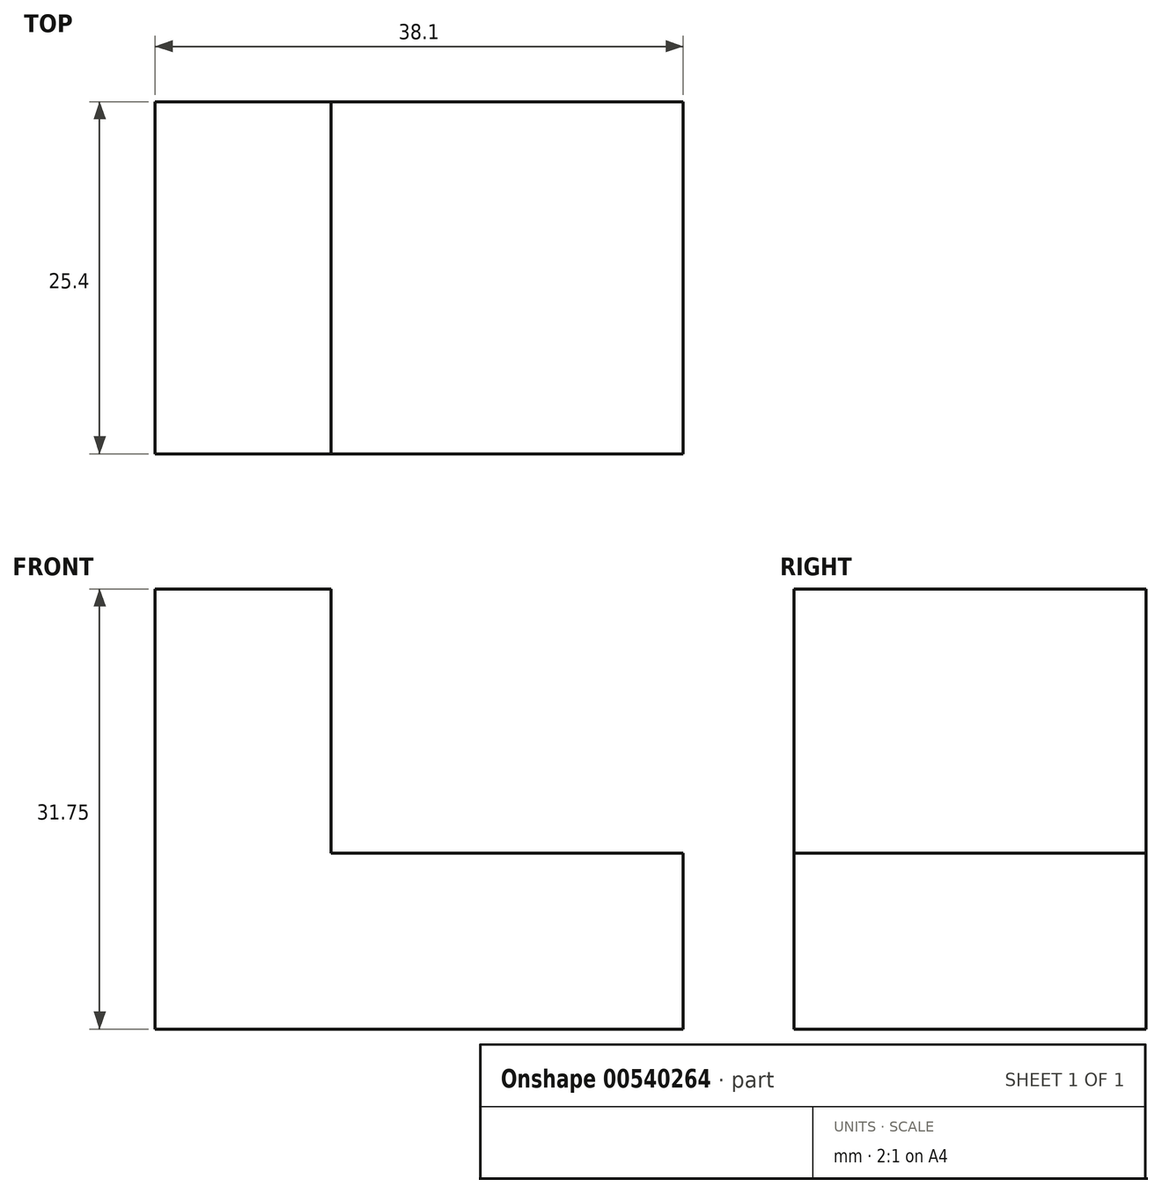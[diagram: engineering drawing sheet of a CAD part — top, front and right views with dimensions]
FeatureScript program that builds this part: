
annotation { "Feature Type Name" : "Feature", "Feature Type Description" : "" }
export const myFeature = defineFeature(function(context is Context, id is Id, definition is map)
    precondition{}
    {
        {
            var Q0;
            Q0=qCreatedBy(makeId("Front.planeOp"),FACE);
            var sketch = newSketch(context, id + "F0", { "sketchPlane" : qUnion([Q0])});
            skLineSegment(sketch, "E0", {"start": v(-68.75, 31.75) * mm, "end": v(-68.75, 0) * mm});
            skLineSegment(sketch, "E1", {"start": v(-68.75, 0) * mm, "end": v(-30.65, 0) * mm});
            skLineSegment(sketch, "E2", {"start": v(-30.65, 0) * mm, "end": v(-30.65, 12.7) * mm});
            skLineSegment(sketch, "E3", {"start": v(-30.65, 12.7) * mm, "end": v(-56.05, 12.7) * mm});
            skLineSegment(sketch, "E4", {"start": v(-56.05, 12.7) * mm, "end": v(-56.05, 31.75) * mm});
            skLineSegment(sketch, "E5", {"start": v(-56.05, 31.75) * mm, "end": v(-68.75, 31.75) * mm});
            skSolve(sketch);
        }
        {
            var Q0;
            Q0=makeQuery(id+"F0.imprint","IMPRINT",FACE,{"disambiguationData":[TD([[makeQuery(id+"F0.imprint","IMPRINT",EDGE,{"derivedFrom":sQuery(id+"F0.wireOp",EDGE,"E0")}),1.0]])]});
            extrude(context, id + "F1", {"entities" : qUnion([Q0]), "depth" : 25.4 * mm, "offsetDistance" : 25.4 * mm});
        }
    });
